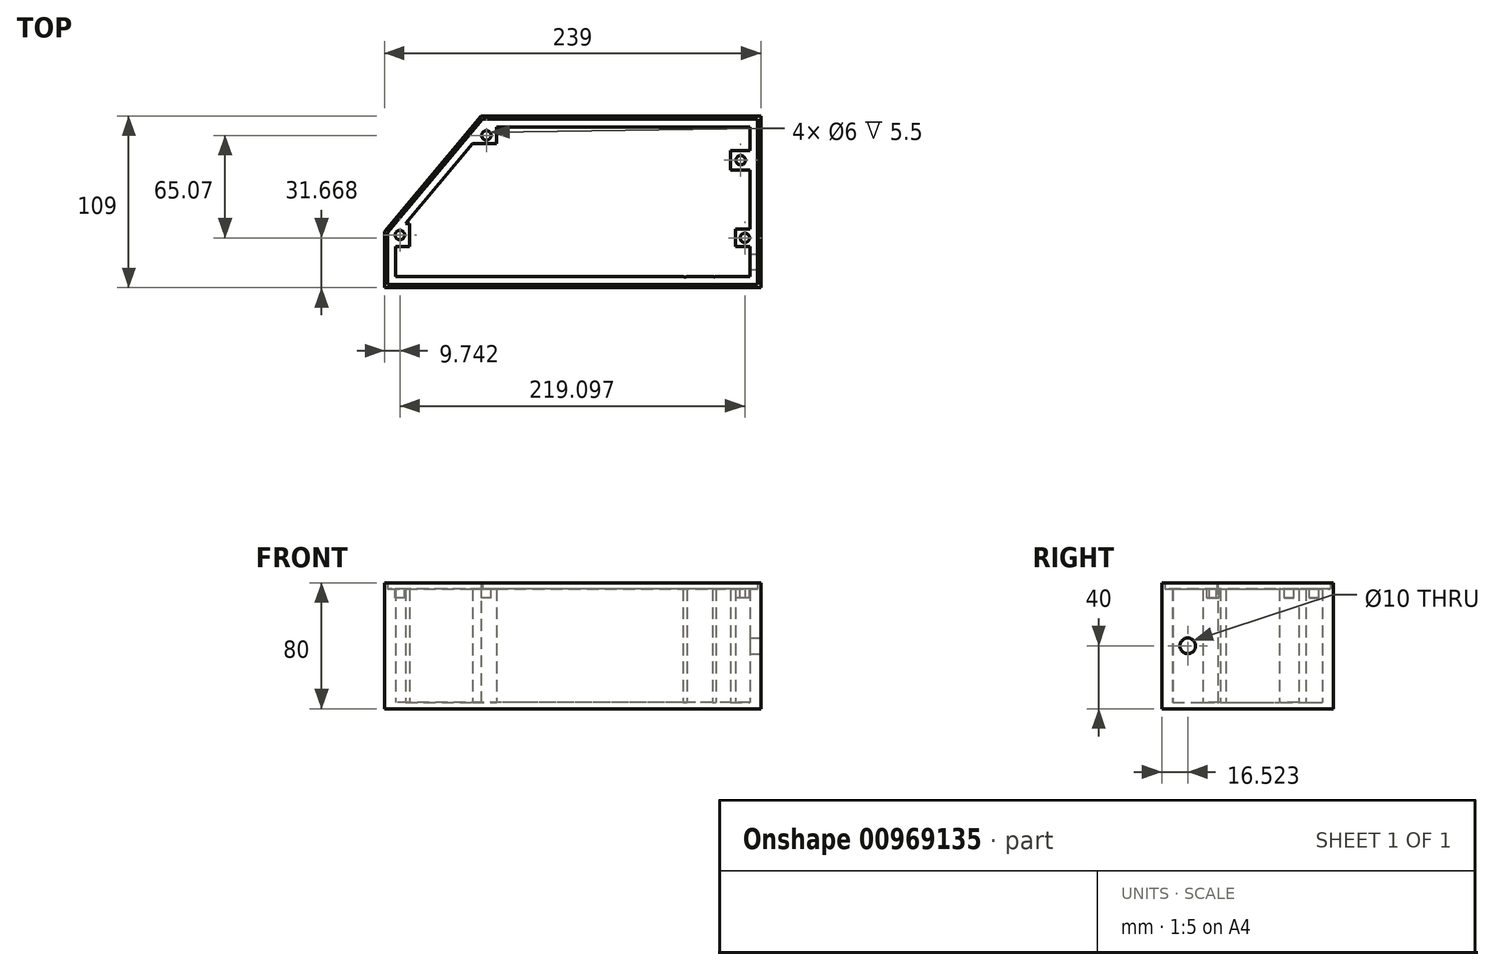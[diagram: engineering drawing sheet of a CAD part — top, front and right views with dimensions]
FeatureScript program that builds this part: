
annotation { "Feature Type Name" : "Feature", "Feature Type Description" : "" }
export const myFeature = defineFeature(function(context is Context, id is Id, definition is map)
    precondition{}
    {
        {
            var Q0;
            Q0=qCreatedBy(makeId("Top.planeOp"),FACE);
            var sketch = newSketch(context, id + "F0", { "sketchPlane" : qUnion([Q0])});
            skLineSegment(sketch, "E0", {"start": v(0, 0) * mm, "end": v(-225, 0) * mm});
            skLineSegment(sketch, "E1", {"start": v(0, 0) * mm, "end": v(0, 19.05) * mm});
            skLineSegment(sketch, "E2", {"start": v(-225, 0) * mm, "end": v(-225, 19) * mm});
            skLineSegment(sketch, "E3", {"start": v(-218.6, 33.87) * mm, "end": v(-176.22, 84.48) * mm});
            skLineSegment(sketch, "E4.0", {"start": v(0, 9) * mm, "end": v(-280, 9) * mm});
            skCircle(sketch, "E5.1.0.0", {"center": v(-208.57, 9.3) * mm, "radius": 9.1 * mm});
            skLineSegment(sketch, "E5.direction1", {"start": v(-231, 9) * mm, "end": v(-212.5, 9) * mm, "construction": true});
            skLineSegment(sketch, "E6.direction1", {"start": v(-221.75, 24.44) * mm, "end": v(-203.25, 24.44) * mm, "construction": true});
            skLineSegment(sketch, "E7.0", {"start": v(0, 95) * mm, "end": v(-160.95, 95) * mm});
            skLineSegment(sketch, "E8.0", {"start": v(-232, 28.77) * mm, "end": v(-170.67, 102) * mm});
            skLineSegment(sketch, "E8.1", {"start": v(7, 102) * mm, "end": v(-170.67, 102) * mm});
            skLineSegment(sketch, "E8.2", {"start": v(7, -7) * mm, "end": v(7, 102) * mm});
            skLineSegment(sketch, "E9.0", {"start": v(-232, -7) * mm, "end": v(-232, 28.77) * mm});
            skLineSegment(sketch, "E10.0", {"start": v(7, -7) * mm, "end": v(-232, -7) * mm});
            skLineSegment(sketch, "E11", {"start": v(-218.6, 33.87) * mm, "end": v(-216.07, 33.87) * mm});
            skLineSegment(sketch, "E12", {"start": v(-216.07, 19) * mm, "end": v(-225, 19) * mm});
            skLineSegment(sketch, "E13", {"start": v(-216.07, 19) * mm, "end": v(-216.07, 33.87) * mm});
            skLineSegment(sketch, "E14", {"start": v(0, 30.29) * mm, "end": v(-9.02, 30.29) * mm});
            skLineSegment(sketch, "E15", {"start": v(-9.02, 30.29) * mm, "end": v(-9.02, 19.05) * mm});
            skLineSegment(sketch, "E16", {"start": v(-9.02, 19.05) * mm, "end": v(0, 19.05) * mm});
            skLineSegment(sketch, "E17.trimOffspring", {"start": v(0, 30.29) * mm, "end": v(0, 67.76) * mm});
            skLineSegment(sketch, "E18", {"start": v(-176.22, 84.48) * mm, "end": v(-160.95, 84.48) * mm});
            skLineSegment(sketch, "E19", {"start": v(-160.95, 84.48) * mm, "end": v(-160.95, 95) * mm});
            skLineSegment(sketch, "E20", {"start": v(0, 80.25) * mm, "end": v(-12.43, 80.2) * mm});
            skLineSegment(sketch, "E21", {"start": v(-12.43, 80.2) * mm, "end": v(-12.38, 67.76) * mm});
            skLineSegment(sketch, "E22", {"start": v(-12.38, 67.76) * mm, "end": v(0, 67.76) * mm});
            skLineSegment(sketch, "E23.trimOffspring", {"start": v(0, 80.25) * mm, "end": v(0, 95) * mm});
            skCircle(sketch, "E24.0", {"center": v(-208.57, 9.3) * mm, "radius": 9.3 * mm});
            skCircle(sketch, "E25.1.0.0", {"center": v(-189.97, 9.3) * mm, "radius": 9.1 * mm});
            skCircle(sketch, "E26.0", {"center": v(-189.97, 9.3) * mm, "radius": 9.3 * mm});
            skCircle(sketch, "E27.1.0.0", {"center": v(-171.37, 9.3) * mm, "radius": 9.1 * mm});
            skCircle(sketch, "E28.0", {"center": v(-171.37, 9.3) * mm, "radius": 9.3 * mm});
            skCircle(sketch, "E29.1.0.0", {"center": v(-152.77, 9.3) * mm, "radius": 9.1 * mm});
            skCircle(sketch, "E30.0", {"center": v(-152.77, 9.3) * mm, "radius": 9.3 * mm});
            skCircle(sketch, "E31.1.0.0", {"center": v(-134.17, 9.3) * mm, "radius": 9.1 * mm});
            skCircle(sketch, "E32.0", {"center": v(-134.17, 9.3) * mm, "radius": 9.3 * mm});
            skCircle(sketch, "E33.1.0.0", {"center": v(-115.57, 9.3) * mm, "radius": 9.1 * mm});
            skCircle(sketch, "E34.0", {"center": v(-115.57, 9.3) * mm, "radius": 9.3 * mm});
            skCircle(sketch, "E35.1.0.0", {"center": v(-96.97, 9.3) * mm, "radius": 9.1 * mm});
            skCircle(sketch, "E36.0", {"center": v(-96.97, 9.3) * mm, "radius": 9.3 * mm});
            skCircle(sketch, "E37.1.0.0", {"center": v(-78.37, 9.3) * mm, "radius": 9.1 * mm});
            skCircle(sketch, "E38.0", {"center": v(-78.37, 9.3) * mm, "radius": 9.3 * mm});
            skCircle(sketch, "E39.1.0.0", {"center": v(-59.77, 9.3) * mm, "radius": 9.1 * mm});
            skCircle(sketch, "E40.0", {"center": v(-59.77, 9.3) * mm, "radius": 9.3 * mm});
            skCircle(sketch, "E41.1.0.0", {"center": v(-41.17, 9.2) * mm, "radius": 9.1 * mm});
            skCircle(sketch, "E42.0", {"center": v(-41.17, 9.2) * mm, "radius": 9.3 * mm});
            skCircle(sketch, "E43.1.0.0", {"center": v(-22.57, 9.22) * mm, "radius": 9.1 * mm});
            skCircle(sketch, "E44.0", {"center": v(-22.57, 9.22) * mm, "radius": 9.3 * mm});
            skCircle(sketch, "E45.1.0.0", {"center": v(-199.3, 25.42) * mm, "radius": 9.1 * mm});
            skCircle(sketch, "E46.0", {"center": v(-199.3, 25.42) * mm, "radius": 9.3 * mm});
            skCircle(sketch, "E47.1.0.0", {"center": v(-180.7, 25.34) * mm, "radius": 9.1 * mm});
            skCircle(sketch, "E48.0", {"center": v(-180.7, 25.34) * mm, "radius": 9.3 * mm});
            skCircle(sketch, "E49.1.0.0", {"center": v(-162.1, 25.34) * mm, "radius": 9.1 * mm});
            skCircle(sketch, "E50.0", {"center": v(-162.1, 25.34) * mm, "radius": 9.3 * mm});
            skCircle(sketch, "E51.1.0.0", {"center": v(-143.5, 25.34) * mm, "radius": 9.1 * mm});
            skCircle(sketch, "E52.0", {"center": v(-143.5, 25.34) * mm, "radius": 9.3 * mm});
            skCircle(sketch, "E53.1.0.0", {"center": v(-124.9, 25.34) * mm, "radius": 9.1 * mm});
            skCircle(sketch, "E54.0", {"center": v(-124.9, 25.34) * mm, "radius": 9.3 * mm});
            skCircle(sketch, "E55.1.0.0", {"center": v(-106.3, 25.34) * mm, "radius": 9.1 * mm});
            skCircle(sketch, "E56.0", {"center": v(-106.3, 25.34) * mm, "radius": 9.3 * mm});
            skCircle(sketch, "E57.1.0.0", {"center": v(-87.7, 25.34) * mm, "radius": 9.1 * mm});
            skCircle(sketch, "E58.0", {"center": v(-87.7, 25.34) * mm, "radius": 9.3 * mm});
            skCircle(sketch, "E59.1.0.0", {"center": v(-69.1, 25.34) * mm, "radius": 9.1 * mm});
            skCircle(sketch, "E60.0", {"center": v(-69.1, 25.34) * mm, "radius": 9.3 * mm});
            skCircle(sketch, "E61.1.0.0", {"center": v(-50.5, 25.34) * mm, "radius": 9.1 * mm});
            skCircle(sketch, "E62.0", {"center": v(-50.5, 25.34) * mm, "radius": 9.3 * mm});
            skCircle(sketch, "E63.1.0.0", {"center": v(-31.9, 25.31) * mm, "radius": 9.1 * mm});
            skCircle(sketch, "E64.0", {"center": v(-31.9, 25.31) * mm, "radius": 9.3 * mm});
            skCircle(sketch, "E65.1.0.0", {"center": v(-189.97, 41.52) * mm, "radius": 9.1 * mm});
            skCircle(sketch, "E66.0", {"center": v(-189.97, 41.52) * mm, "radius": 9.3 * mm});
            skCircle(sketch, "E67.1.0.0", {"center": v(-171.37, 41.52) * mm, "radius": 9.1 * mm});
            skCircle(sketch, "E68.0", {"center": v(-171.37, 41.52) * mm, "radius": 9.3 * mm});
            skCircle(sketch, "E69.1.0.0", {"center": v(-152.77, 41.52) * mm, "radius": 9.1 * mm});
            skCircle(sketch, "E70.0", {"center": v(-152.77, 41.52) * mm, "radius": 9.3 * mm});
            skCircle(sketch, "E71.1.0.0", {"center": v(-134.17, 41.52) * mm, "radius": 9.1 * mm});
            skCircle(sketch, "E72.0", {"center": v(-134.17, 41.52) * mm, "radius": 9.3 * mm});
            skCircle(sketch, "E73.1.0.0", {"center": v(-115.57, 41.52) * mm, "radius": 9.1 * mm});
            skCircle(sketch, "E74.0", {"center": v(-115.57, 41.52) * mm, "radius": 9.3 * mm});
            skCircle(sketch, "E75.1.0.0", {"center": v(-96.97, 41.52) * mm, "radius": 9.1 * mm});
            skCircle(sketch, "E76.0", {"center": v(-96.97, 41.52) * mm, "radius": 9.3 * mm});
            skCircle(sketch, "E77.1.0.0", {"center": v(-78.37, 41.49) * mm, "radius": 9.1 * mm});
            skCircle(sketch, "E78.0", {"center": v(-78.37, 41.49) * mm, "radius": 9.3 * mm});
            skCircle(sketch, "E79.1.0.0", {"center": v(-59.77, 41.46) * mm, "radius": 9.1 * mm});
            skCircle(sketch, "E80.0", {"center": v(-59.77, 41.46) * mm, "radius": 9.3 * mm});
            skCircle(sketch, "E81.1.0.0", {"center": v(-41.17, 41.43) * mm, "radius": 9.1 * mm});
            skCircle(sketch, "E82.0", {"center": v(-41.17, 41.43) * mm, "radius": 9.3 * mm});
            skCircle(sketch, "E83.1.0.0", {"center": v(-22.57, 41.4) * mm, "radius": 9.1 * mm});
            skCircle(sketch, "E84.0", {"center": v(-22.57, 41.4) * mm, "radius": 9.3 * mm});
            skCircle(sketch, "E85.1.0.0", {"center": v(-180.64, 57.61) * mm, "radius": 9.1 * mm});
            skCircle(sketch, "E86.0", {"center": v(-180.64, 57.61) * mm, "radius": 9.3 * mm});
            skCircle(sketch, "E87.1.0.0", {"center": v(-162.04, 57.61) * mm, "radius": 9.1 * mm});
            skCircle(sketch, "E88.0", {"center": v(-162.04, 57.61) * mm, "radius": 9.3 * mm});
            skCircle(sketch, "E89.1.0.0", {"center": v(-143.44, 57.61) * mm, "radius": 9.1 * mm});
            skCircle(sketch, "E90.0", {"center": v(-143.44, 57.61) * mm, "radius": 9.3 * mm});
            skCircle(sketch, "E91.1.0.0", {"center": v(-124.84, 57.61) * mm, "radius": 9.1 * mm});
            skCircle(sketch, "E92.0", {"center": v(-124.84, 57.61) * mm, "radius": 9.3 * mm});
            skCircle(sketch, "E93.1.0.0", {"center": v(-106.24, 57.61) * mm, "radius": 9.1 * mm});
            skCircle(sketch, "E94.0", {"center": v(-106.24, 57.61) * mm, "radius": 9.3 * mm});
            skCircle(sketch, "E95.1.0.0", {"center": v(-87.64, 57.61) * mm, "radius": 9.1 * mm});
            skCircle(sketch, "E96.0", {"center": v(-87.64, 57.61) * mm, "radius": 9.3 * mm});
            skCircle(sketch, "E97.1.0.0", {"center": v(-69.04, 57.58) * mm, "radius": 9.1 * mm});
            skCircle(sketch, "E98.0", {"center": v(-69.04, 57.58) * mm, "radius": 9.3 * mm});
            skCircle(sketch, "E99.1.0.0", {"center": v(-50.44, 57.56) * mm, "radius": 9.1 * mm});
            skCircle(sketch, "E100.0", {"center": v(-50.44, 57.56) * mm, "radius": 9.3 * mm});
            skCircle(sketch, "E101.1.0.0", {"center": v(-31.84, 57.53) * mm, "radius": 9.1 * mm});
            skCircle(sketch, "E102.0", {"center": v(-31.84, 57.53) * mm, "radius": 9.3 * mm});
            skCircle(sketch, "E103.1.0.0", {"center": v(-171.34, 73.71) * mm, "radius": 9.1 * mm});
            skCircle(sketch, "E104.0", {"center": v(-171.34, 73.71) * mm, "radius": 9.3 * mm});
            skCircle(sketch, "E105.1.0.0", {"center": v(-152.74, 73.63) * mm, "radius": 9.1 * mm});
            skCircle(sketch, "E106.0", {"center": v(-152.74, 73.63) * mm, "radius": 9.3 * mm});
            skCircle(sketch, "E107.1.0.0", {"center": v(-134.14, 73.63) * mm, "radius": 9.1 * mm});
            skCircle(sketch, "E108.0", {"center": v(-134.14, 73.63) * mm, "radius": 9.3 * mm});
            skCircle(sketch, "E109.1.0.0", {"center": v(-115.54, 73.63) * mm, "radius": 9.1 * mm});
            skCircle(sketch, "E110.0", {"center": v(-115.54, 73.63) * mm, "radius": 9.3 * mm});
            skCircle(sketch, "E111.1.0.0", {"center": v(-96.94, 73.63) * mm, "radius": 9.1 * mm});
            skCircle(sketch, "E112.0", {"center": v(-96.94, 73.63) * mm, "radius": 9.3 * mm});
            skCircle(sketch, "E113.1.0.0", {"center": v(-78.34, 73.63) * mm, "radius": 9.1 * mm});
            skCircle(sketch, "E114.0", {"center": v(-78.34, 73.63) * mm, "radius": 9.3 * mm});
            skCircle(sketch, "E115.1.0.0", {"center": v(-59.74, 73.63) * mm, "radius": 9.1 * mm});
            skCircle(sketch, "E116.0", {"center": v(-59.74, 73.63) * mm, "radius": 9.3 * mm});
            skCircle(sketch, "E117.1.0.0", {"center": v(-41.14, 73.63) * mm, "radius": 9.1 * mm});
            skCircle(sketch, "E118.0", {"center": v(-41.14, 73.63) * mm, "radius": 9.3 * mm});
            skSolve(sketch);
        }
        {
            var Q0;
            Q0=qSketchRegion(id+"F0",true);
            extrude(context, id + "F1", {"entities" : qUnion([Q0]), "depth" : 72 * mm, "offsetDistance" : 25 * mm});
        }
        {
            var Q0;
            Q0=qCreatedBy(makeId("Top.planeOp"),FACE);
            var sketch = newSketch(context, id + "F2", { "sketchPlane" : qUnion([Q0])});
            skLineSegment(sketch, "E119.0.0", {"start": v(-232, 28.77) * mm, "end": v(-170.67, 102) * mm});
            skLineSegment(sketch, "E119.0.1", {"start": v(-170.67, 102) * mm, "end": v(7, 102) * mm});
            skLineSegment(sketch, "E119.0.2", {"start": v(7, 102) * mm, "end": v(7, -7) * mm});
            skLineSegment(sketch, "E119.0.3", {"start": v(7, -7) * mm, "end": v(-232, -7) * mm});
            skLineSegment(sketch, "E119.0.4", {"start": v(-232, -7) * mm, "end": v(-232, 28.77) * mm});
            skSolve(sketch);
        }
        {
            var Q0;
            Q0=qSketchRegion(id+"F2",true);
            extrude(context, id + "F3", {"entities" : qUnion([Q0]), "operationType" : NewBodyOperationType.ADD, "oppositeDirection" : true, "depth" : 4 * mm, "offsetDistance" : 25 * mm});
        }
        {
            var Q0;
            Q0=makeQuery(id+"F1.opExtrude","CAP_FACE",FACE,{"disambiguationData":[OSD([sQuery(id+"F0.wireOp",EDGE,"E0"),sQuery(id+"F0.wireOp",EDGE,"E1"),sQuery(id+"F0.wireOp",EDGE,"E2"),sQuery(id+"F0.wireOp",EDGE,"E3"),sQuery(id+"F0.wireOp",EDGE,"E7.0"),sQuery(id+"F0.wireOp",EDGE,"E8.0"),sQuery(id+"F0.wireOp",EDGE,"E8.1"),sQuery(id+"F0.wireOp",EDGE,"E8.2"),sQuery(id+"F0.wireOp",EDGE,"E9.0"),sQuery(id+"F0.wireOp",EDGE,"E10.0"),sQuery(id+"F0.wireOp",EDGE,"E11"),sQuery(id+"F0.wireOp",EDGE,"E12"),sQuery(id+"F0.wireOp",EDGE,"E13"),sQuery(id+"F0.wireOp",EDGE,"E14"),sQuery(id+"F0.wireOp",EDGE,"E15"),sQuery(id+"F0.wireOp",EDGE,"E16"),sQuery(id+"F0.wireOp",EDGE,"E17.trimOffspring"),sQuery(id+"F0.wireOp",EDGE,"E18"),sQuery(id+"F0.wireOp",EDGE,"E19"),sQuery(id+"F0.wireOp",EDGE,"E20"),sQuery(id+"F0.wireOp",EDGE,"E21"),sQuery(id+"F0.wireOp",EDGE,"E22"),sQuery(id+"F0.wireOp",EDGE,"E23.trimOffspring")])],"isStart":false});
            var sketch = newSketch(context, id + "F4", { "sketchPlane" : qUnion([Q0])});
            skLineSegment(sketch, "E120.0.0", {"start": v(-170.67, 102) * mm, "end": v(-232, 28.77) * mm});
            skLineSegment(sketch, "E120.0.1", {"start": v(-232, 28.77) * mm, "end": v(-232, -7) * mm});
            skLineSegment(sketch, "E120.0.2", {"start": v(-232, -7) * mm, "end": v(7, -7) * mm});
            skLineSegment(sketch, "E120.0.3", {"start": v(7, -7) * mm, "end": v(7, 102) * mm});
            skLineSegment(sketch, "E120.0.4", {"start": v(7, 102) * mm, "end": v(-170.67, 102) * mm});
            skLineSegment(sketch, "E121.0", {"start": v(-230, 28.04) * mm, "end": v(-230, -5) * mm});
            skLineSegment(sketch, "E121.1", {"start": v(-169.74, 100) * mm, "end": v(-230, 28.04) * mm});
            skLineSegment(sketch, "E121.2", {"start": v(-230, -5) * mm, "end": v(5, -5) * mm});
            skLineSegment(sketch, "E121.3", {"start": v(5, -5) * mm, "end": v(5, 100) * mm});
            skLineSegment(sketch, "E121.4", {"start": v(5, 100) * mm, "end": v(-169.74, 100) * mm});
            skSolve(sketch);
        }
        {
            var Q0;
            Q0=makeQuery(id+"F4.imprint","IMPRINT",FACE,{"disambiguationData":[TD([[makeQuery(id+"F4.imprint","IMPRINT",EDGE,{"derivedFrom":sQuery(id+"F4.wireOp",EDGE,"E120.0.0")}),-1.0]])]});
            extrude(context, id + "F5", {"entities" : qUnion([Q0]), "operationType" : NewBodyOperationType.ADD, "depth" : 4 * mm, "offsetDistance" : 25 * mm});
        }
        {
            var Q0;
            Q0=makeQuery(id+"F5.boolean.opBoolean","MERGE",FACE,{"derivedFrom":[makeQuery(id+"F3.boolean.opBoolean","MERGE",FACE,{"derivedFrom":[makeQuery(id+"F1.opExtrude","SWEPT_FACE",FACE,{"disambiguationData":[OSD([sQuery(id+"F0.wireOp",EDGE,"E8.2")])]}),makeQuery(id+"F3.opExtrude","SWEPT_FACE",FACE,{"disambiguationData":[OSD([sQuery(id+"F2.wireOp",EDGE,"E119.0.2")])]})]}),makeQuery(id+"F5.opExtrude","SWEPT_FACE",FACE,{"disambiguationData":[OSD([sQuery(id+"F4.wireOp",EDGE,"E120.0.3")])]})]});
            var sketch = newSketch(context, id + "F6", { "sketchPlane" : qUnion([Q0])});
            skLineSegment(sketch, "E122.0.0", {"start": v(19.05, 0) * mm, "end": v(0, 0) * mm});
            skLineSegment(sketch, "E122.0.1", {"start": v(0, 0) * mm, "end": v(0, 72) * mm});
            skLineSegment(sketch, "E122.0.2", {"start": v(0, 72) * mm, "end": v(19.05, 72) * mm});
            skLineSegment(sketch, "E122.0.3", {"start": v(19.05, 72) * mm, "end": v(19.05, 0) * mm});
            skLineSegment(sketch, "E123", {"start": v(0, 36) * mm, "end": v(19.05, 36) * mm});
            skCircle(sketch, "E124", {"center": v(9.52, 36) * mm, "radius": 5 * mm});
            skSolve(sketch);
        }
        {
            var Q0;
            {var subQ0=sQuery(id+"F6.wireOp",EDGE,"E124");var subQ1=sQuery(id+"F6.wireOp",EDGE,"E123");var subQ2=makeQuery(id+"F6.imprint","INTERSECT",VERTEX,{"disambiguationData":[OD(0.0)],"derivedFrom":[subQ1,subQ0]});Q0=makeQuery(id+"F6.imprint","IMPRINT",FACE,{"disambiguationData":[TD([[makeQuery(id+"F6.imprint","IMPRINT",EDGE,{"disambiguationData":[TD([[subQ2,-1.0]])],"derivedFrom":subQ1}),1.0]])]});}
            var Q1;
            {var subQ0=sQuery(id+"F6.wireOp",EDGE,"E124");var subQ1=sQuery(id+"F6.wireOp",EDGE,"E123");var subQ2=makeQuery(id+"F6.imprint","INTERSECT",VERTEX,{"disambiguationData":[OD(0.0)],"derivedFrom":[subQ1,subQ0]});Q1=makeQuery(id+"F6.imprint","IMPRINT",FACE,{"disambiguationData":[TD([[makeQuery(id+"F6.imprint","IMPRINT",EDGE,{"disambiguationData":[TD([[subQ2,-1.0]])],"derivedFrom":subQ1}),-1.0]])]});}
            extrude(context, id + "F7", {"entities" : qUnion([Q0, Q1]), "operationType" : NewBodyOperationType.REMOVE, "oppositeDirection" : true, "depth" : 25 * mm, "offsetDistance" : 25 * mm});
        }
        {
            var Q0;
            Q0=makeQuery(id+"F1.opExtrude","CAP_FACE",FACE,{"disambiguationData":[OSD([sQuery(id+"F0.wireOp",EDGE,"E0"),sQuery(id+"F0.wireOp",EDGE,"E1"),sQuery(id+"F0.wireOp",EDGE,"E2"),sQuery(id+"F0.wireOp",EDGE,"E3"),sQuery(id+"F0.wireOp",EDGE,"E7.0"),sQuery(id+"F0.wireOp",EDGE,"E8.0"),sQuery(id+"F0.wireOp",EDGE,"E8.1"),sQuery(id+"F0.wireOp",EDGE,"E8.2"),sQuery(id+"F0.wireOp",EDGE,"E9.0"),sQuery(id+"F0.wireOp",EDGE,"E10.0"),sQuery(id+"F0.wireOp",EDGE,"E11"),sQuery(id+"F0.wireOp",EDGE,"E12"),sQuery(id+"F0.wireOp",EDGE,"E13"),sQuery(id+"F0.wireOp",EDGE,"E14"),sQuery(id+"F0.wireOp",EDGE,"E15"),sQuery(id+"F0.wireOp",EDGE,"E16"),sQuery(id+"F0.wireOp",EDGE,"E17.trimOffspring"),sQuery(id+"F0.wireOp",EDGE,"E18"),sQuery(id+"F0.wireOp",EDGE,"E19"),sQuery(id+"F0.wireOp",EDGE,"E20"),sQuery(id+"F0.wireOp",EDGE,"E21"),sQuery(id+"F0.wireOp",EDGE,"E22"),sQuery(id+"F0.wireOp",EDGE,"E23.trimOffspring")])],"isStart":false});
            var sketch = newSketch(context, id + "F8", { "sketchPlane" : qUnion([Q0])});
            skCircle(sketch, "E125", {"center": v(-167.3, 89.74) * mm, "radius": 3 * mm});
            skPoint(sketch, "E125.centerSnap0", {"position": v(-160.95, 89.74) * mm});
            skCircle(sketch, "E126", {"center": v(-222.26, 26.44) * mm, "radius": 3 * mm});
            skPoint(sketch, "E126.centerSnap0", {"position": v(-216.07, 26.44) * mm});
            skCircle(sketch, "E127", {"center": v(-5.79, 73.98) * mm, "radius": 3 * mm});
            skPoint(sketch, "E127.centerSnap0", {"position": v(-12.4, 73.98) * mm});
            skCircle(sketch, "E128", {"center": v(-3.16, 24.67) * mm, "radius": 3 * mm});
            skPoint(sketch, "E128.centerSnap0", {"position": v(-9.02, 24.67) * mm});
            skLineSegment(sketch, "E129", {"start": v(0, 0) * mm, "end": v(-27.6, 0) * mm});
            skLineSegment(sketch, "E130", {"start": v(0, 0) * mm, "end": v(0, 8.28) * mm});
            skSolve(sketch);
        }
        {
            var Q0;
            Q0=qSketchRegion(id+"F8",true);
            extrude(context, id + "F9", {"entities" : qUnion([Q0]), "operationType" : NewBodyOperationType.REMOVE, "oppositeDirection" : true, "depth" : 5.5 * mm, "offsetDistance" : 25 * mm});
        }
    });
